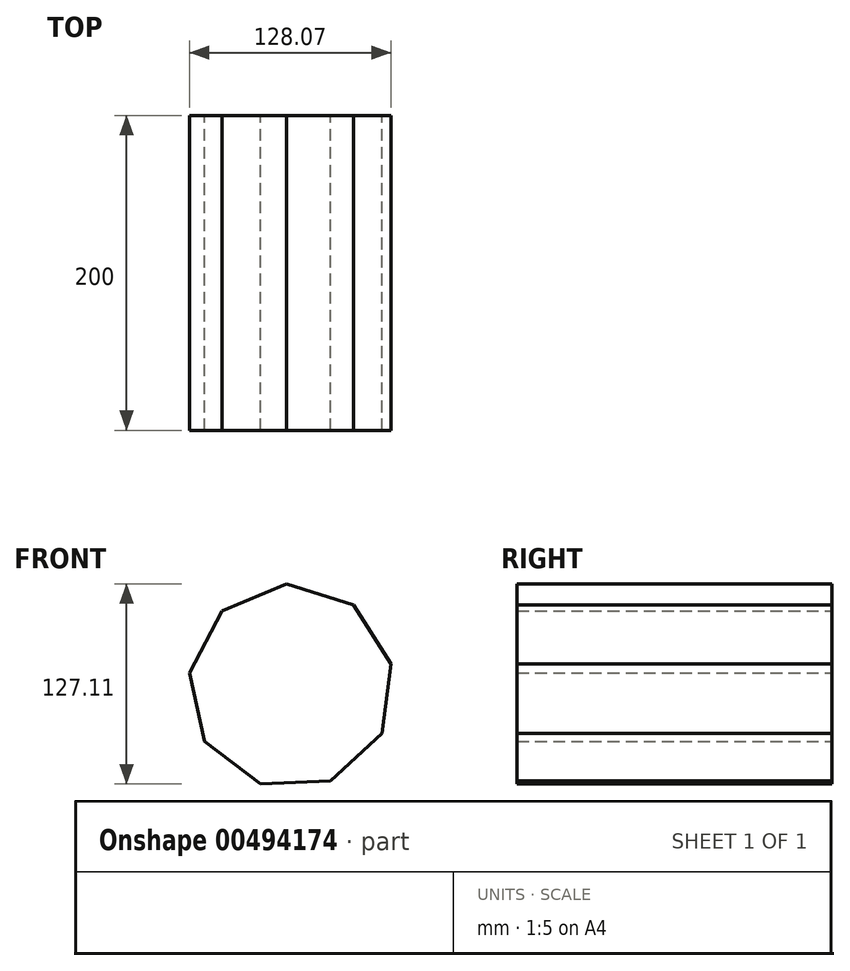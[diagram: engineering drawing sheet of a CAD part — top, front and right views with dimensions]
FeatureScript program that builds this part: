
annotation { "Feature Type Name" : "Feature", "Feature Type Description" : "" }
export const myFeature = defineFeature(function(context is Context, id is Id, definition is map)
    precondition{}
    {
        {
            var Q0;
            Q0=qCreatedBy(makeId("Front.planeOp"),FACE);
            var sketch = newSketch(context, id + "F0", { "sketchPlane" : qUnion([Q0])});
            skCircle(sketch, "E0.cCircle", {"center": v(0, 0) * mm, "radius": 65.09 * mm, "construction": true});
            skLineSegment(sketch, "E0.0", {"start": v(-44.01, 47.95) * mm, "end": v(-2.9, 65.02) * mm});
            skLineSegment(sketch, "E0.1", {"start": v(-2.9, 65.02) * mm, "end": v(39.58, 51.67) * mm});
            skLineSegment(sketch, "E0.2", {"start": v(39.58, 51.67) * mm, "end": v(63.53, 14.14) * mm});
            skLineSegment(sketch, "E0.3", {"start": v(63.53, 14.14) * mm, "end": v(57.76, -30) * mm});
            skLineSegment(sketch, "E0.4", {"start": v(57.76, -30) * mm, "end": v(24.96, -60.1) * mm});
            skLineSegment(sketch, "E0.5", {"start": v(24.96, -60.1) * mm, "end": v(-19.52, -62.1) * mm});
            skLineSegment(sketch, "E0.6", {"start": v(-19.52, -62.1) * mm, "end": v(-54.86, -35.02) * mm});
            skLineSegment(sketch, "E0.7", {"start": v(-54.86, -35.02) * mm, "end": v(-64.54, 8.44) * mm});
            skLineSegment(sketch, "E0.8", {"start": v(-64.54, 8.44) * mm, "end": v(-44.01, 47.95) * mm});
            skSolve(sketch);
        }
        {
            var Q0;
            Q0=makeQuery(id+"F0.imprint","IMPRINT",FACE,{"disambiguationData":[TD([[makeQuery(id+"F0.imprint","IMPRINT",EDGE,{"derivedFrom":sQuery(id+"F0.wireOp",EDGE,"E0.0")}),-1.0]])]});
            extrude(context, id + "F1", {"entities" : qUnion([Q0]), "endBound" : BoundingType.SYMMETRIC, "depth" : 200 * mm});
        }
    });
